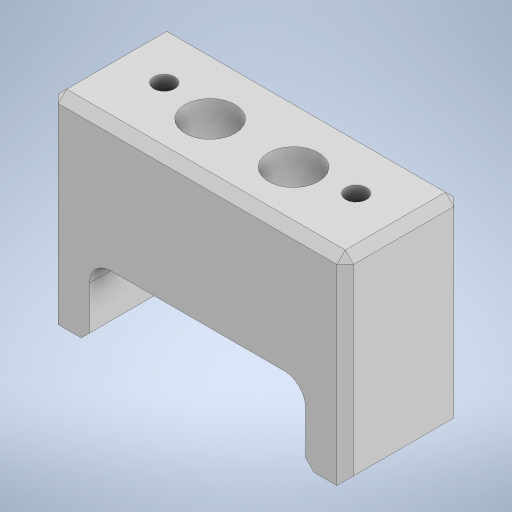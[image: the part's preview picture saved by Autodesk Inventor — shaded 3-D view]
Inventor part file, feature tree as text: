
AUTODESK INVENTOR PART (.ipt)
format: ipt  version: 2023 (Build 270158000, 158)  size: 343,040 bytes
history: native  units: in
note: dims shown in document units (in); Inventor stores cm internally (conversion verified against a paired STEP export)
features: extrude x8, sketch x6, plane x1, thicken_offset x1, chamfer x1
ambient origin geometry x8: Origin, YZ Plane, XZ Plane, XY Plane, X Axis, Y Axis, Z Axis, Center Point
bodies: Solid1 (feature_tree)
feature tree (17):
  sketch  "Sketch1"  dims[d0=0.7874in d1=2.3622in]
  extrude  "Extrusion1"  Depth=2.3622in
  extrude  "Extrusion3"  Depth=0.0197in
  extrude  "Extrusion4"  Depth=0.0197in
  plane  "Work Plane3"
  extrude  "Extrusion5"  Depth=1.811in
  extrude  "Extrusion2"  Depth=2.7874in
  extrude  "Extrusion8"  Depth=0.3937in TaperAngle=0.0deg
  thicken_offset  "Thicken1"
  extrude  "Extrusion11"  Depth=0.3937in TaperAngle=0.0deg
  extrude  "Extrusion12"  Depth=1.1969in TaperAngle=0.0deg
  chamfer  "Chamfer1"  Distance=0.3937in
  sketch  "Sketch2"  dims[d2=0.0197in d3=0.0197in]
  sketch  "Sketch3"  dims[d4=0.0197in d5=0.0197in]
  sketch  "Sketch8"  dims[d6=0.1969in d7=1.811in]
  sketch  "Sketch11"  dims[d9=2.7874in d10=1.1811in]
  sketch  "Sketch12"  dims[d11=1.1969in d12=0.0in d13=1.3937in d14=0.0in d15=1.7062in d16=0.1969in d17=0.0in d18=0.0in d19=1.7062in d20=1.1969in d21=0.0in d22=0.0in d27=0.3937in d28=0.0in d31=0.3937in d32=0.0in d44=1.3937in d64=0.0394in d65=0.1181in d66=135.0deg d67=0.0787in d69=0.1358in d71=0.689in d72=0.2819in d73=0.0935in d74=0.0525in d75=0.0953in d76=0.6063in d77=0.3937in d78=0.3937in d79=0.0in d80=0.0394in d81=0.0394in d82=0.2362in d94=2.0394in d95=0.689in d96=0.2in d98=0.7874in d99=0.4724in d100=0.3937in d101=0.0in d102=0.0787in d103=0.0787in d104=45.0deg d105=0.0787in d106=0.0in d107=0.0in d109=0.0787in]
